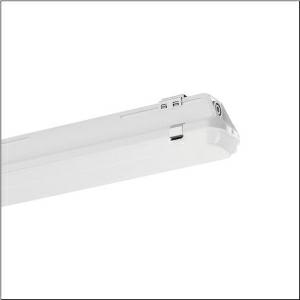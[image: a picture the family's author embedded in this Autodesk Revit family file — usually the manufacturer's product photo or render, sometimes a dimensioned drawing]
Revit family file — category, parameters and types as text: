
# Revit family: monsun_11_51fp10dp460l
name_source: partatom
category: Lighting Fixtures
units: mm (PartAtom-declared; Revit-internal decimal feet)

## family parameters
Cut with Voids When Loaded = No
Host = Face
Light Source = No
Part Type = Normal
Room Calculation Point = No
Round Connector Dimension = Use Diameter
Shared = No

## types (1)
- --- (1 x LED, 6110 lm, 31.8 W, 4000K)
    Apparent Load = 32 VA
    CIE Flux Codes = 47 77 93 94 100
    Color Rendering = 80
    Color Temperature = 4000K
    Default Elevation = 1800 mm
    Description = Monsun 11, damp-proof luminaire, chain hanger, primary optical cover: enclosure, of PMMA, light emission: direct distribution, primary light characteristic: symmetric, installation type: suspended mounting, surface-mounted, horizontal mounting, vertical mounting, LED, rated luminous flux: 6.110lm, luminous efficacy: 192lm/W, light colour: 840, colour temperature: 4000K, control gear: DALI 2, with terminal, 5-pole, max. 2.5mm², mains connection: 220..240V, AC, 50/60Hz, rated input power: 32W, luminaire housing, of glass-fibre reinforced polyester, uncoated, bright grey, incl. chain hanger, length: 1.590mm, width: 90mm, height: 88mm, clip for enclosure, of stainless steel (V2A), ceiling mounting element, of stainless steel (V2A), chain hanger, of stainless steel (V2A), protection rating (complete): IP66, insulation class (complete): insulation class I (protective earthing), certification: CE, ENEC, VDE, UKCA, protection symbol: D, impact resistance: IK04, permissible operating ambient temperature: -25..+35°C, standard: EN 50419, EN 60598-2-1, corresponds to IFS (International Featured Standards) requirements for safety and quality in the food industry, for indoor or canopied outdoor use, no direct snow, no direct sun, no direct rain, LABS conformity tested according to VDMA 24364:2018-05, contact your sales advisor before using the luminaires in applications with unclear chemical exposure, large temperature fluctuations or condensation-forming humidity, packaging unit: 1 piece
    Height = 89 mm
    Lamp = 1 x LED
    Lamp Light Flux = 6110 lm
    Lamp Power = 31.8 W
    Lamp count = 1
    Length = 1590 mm
    Luminous efficacy = 192 lm/W
    Manufacturer = Siteco
    ModVariant = No
    Model = 51FP10DP460L
    Mounting Place = Ceiling
    Mounting Type = Surface mounted
    Number of Poles = 1
    OnlyDefault = Yes
    Power Factor = 1
    Product Name = Monsun 11
    Product group = damp-proof luminaire
    ProductGroupID = 300
    Protection Class = Protection class I
    Protection Degree = IP 66
    RLX_Detail_Level = 1
    RLX_Emergency_Light_Flux = 0 lm
    RLX_Emergency_Type = 0
    RLX_Emergency_Type_DB = No
    RlxData = <blob elided: 91993 chars, md5=92595d46>
    Socket = socket
    Standby Power = 0 W
    System Light Flux = 6110 lm
    System Power = 32 W
    Type Comments = factory setting: luminous flux: 100 % | dim-lin: 254 | 221 mA
    Type Image = l_1349237.jpg
    URL = http://relux.com
    VarID = @adj_034025
    Voltage = 0 V
    Weight = 0.00 kg
    Width = 90 mm

## geometry (parser evidence)
native form markers: Blend x4, Sweep x12
no freeform markers — native parametric forms only
